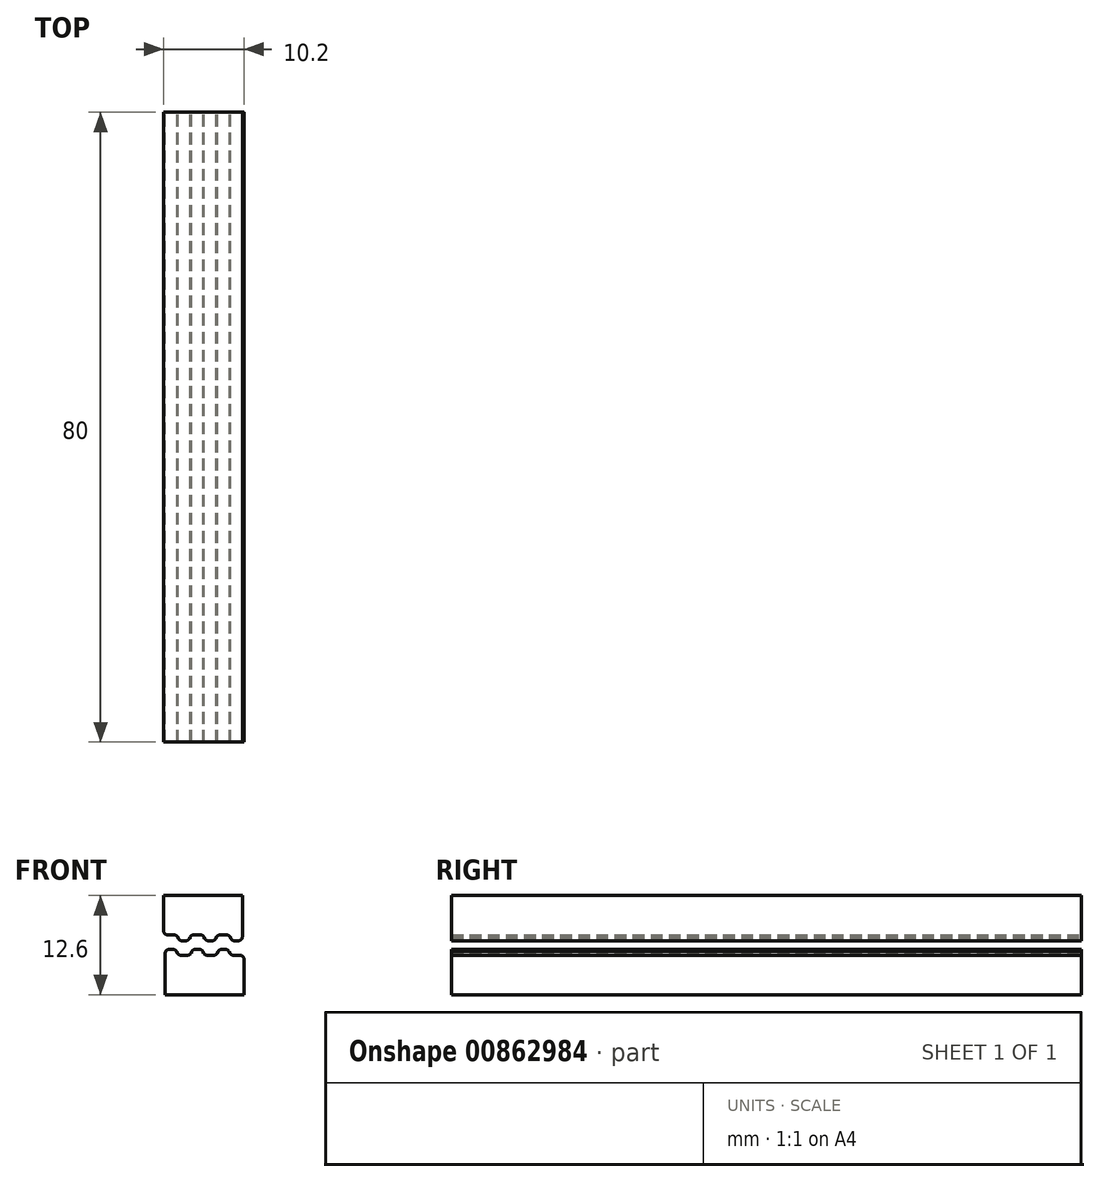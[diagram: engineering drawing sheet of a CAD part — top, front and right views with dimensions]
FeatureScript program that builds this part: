
annotation { "Feature Type Name" : "Feature", "Feature Type Description" : "" }
export const myFeature = defineFeature(function(context is Context, id is Id, definition is map)
    precondition{}
    {
        {
            var Q0;
            Q0=qCreatedBy(makeId("Front.planeOp"),FACE);
            var sketch = newSketch(context, id + "F0", { "sketchPlane" : qUnion([Q0])});
            skLineSegment(sketch, "E0", {"start": v(0, 0) * mm, "end": v(0, 5) * mm});
            skLineSegment(sketch, "E1", {"start": v(2, 5) * mm, "end": v(2.83, 5) * mm});
            skLineSegment(sketch, "E2", {"start": v(10, 4.5) * mm, "end": v(10, 0) * mm});
            skLineSegment(sketch, "E3", {"start": v(10, 0) * mm, "end": v(0, 0) * mm});
            skLineSegment(sketch, "E4.top", {"start": v(0.5, 5.75) * mm, "end": v(1, 5.75) * mm});
            skLineSegment(sketch, "E4.left", {"start": v(0, 5) * mm, "end": v(0, 5.25) * mm});
            skLineSegment(sketch, "E4.right", {"start": v(1.5, 5.25) * mm, "end": v(1.5, 5.5) * mm});
            skLineSegment(sketch, "E5.1.0.0", {"start": v(3.33, 5.25) * mm, "end": v(3.33, 5.5) * mm});
            skLineSegment(sketch, "E5.1.0.1", {"start": v(3.83, 5.75) * mm, "end": v(4.33, 5.75) * mm});
            skLineSegment(sketch, "E5.1.0.2", {"start": v(4.83, 5.25) * mm, "end": v(4.83, 5.5) * mm});
            skLineSegment(sketch, "E5.2.0.0", {"start": v(6.67, 5.25) * mm, "end": v(6.67, 5.5) * mm});
            skLineSegment(sketch, "E5.2.0.1", {"start": v(7.17, 5.75) * mm, "end": v(7.67, 5.75) * mm});
            skLineSegment(sketch, "E5.2.0.2", {"start": v(8.17, 5.25) * mm, "end": v(8.17, 5.5) * mm});
            skLineSegment(sketch, "E5.direction1", {"start": v(0, 5) * mm, "end": v(3.33, 5) * mm, "construction": true});
            skLineSegment(sketch, "E6.trimOffspring", {"start": v(5.33, 5) * mm, "end": v(6.17, 5) * mm});
            skLineSegment(sketch, "E7.trimOffspring", {"start": v(8.67, 5) * mm, "end": v(9.5, 5) * mm});
            skPoint(sketch, "E8.visualSharp", {"position": v(0, 5.75) * mm});
            skArc(sketch, "E8.filletArc", {"start": v(0.5, 5.75) * mm, "mid": v(0.15, 5.6) * mm, "end": v(0, 5.25) * mm});
            skPoint(sketch, "E9.visualSharp", {"position": v(3.33, 5.75) * mm});
            skArc(sketch, "E9.filletArc", {"start": v(3.83, 5.75) * mm, "mid": v(3.48, 5.6) * mm, "end": v(3.33, 5.25) * mm});
            skPoint(sketch, "E10.visualSharp", {"position": v(4.83, 5) * mm});
            skArc(sketch, "E10.filletArc", {"start": v(4.83, 5.5) * mm, "mid": v(4.98, 5.15) * mm, "end": v(5.33, 5) * mm});
            skPoint(sketch, "E11.visualSharp", {"position": v(4.83, 5.75) * mm});
            skArc(sketch, "E11.filletArc", {"start": v(4.83, 5.25) * mm, "mid": v(4.69, 5.6) * mm, "end": v(4.33, 5.75) * mm});
            skPoint(sketch, "E12.visualSharp", {"position": v(6.67, 5) * mm});
            skArc(sketch, "E12.filletArc", {"start": v(6.17, 5) * mm, "mid": v(6.52, 5.15) * mm, "end": v(6.67, 5.5) * mm});
            skPoint(sketch, "E13.visualSharp", {"position": v(6.67, 5.75) * mm});
            skArc(sketch, "E13.filletArc", {"start": v(7.17, 5.75) * mm, "mid": v(6.81, 5.6) * mm, "end": v(6.67, 5.25) * mm});
            skPoint(sketch, "E14.visualSharp", {"position": v(8.17, 5.75) * mm});
            skArc(sketch, "E14.filletArc", {"start": v(8.17, 5.25) * mm, "mid": v(8.02, 5.6) * mm, "end": v(7.67, 5.75) * mm});
            skPoint(sketch, "E15.visualSharp", {"position": v(8.17, 5) * mm});
            skArc(sketch, "E15.filletArc", {"start": v(8.17, 5.5) * mm, "mid": v(8.31, 5.15) * mm, "end": v(8.67, 5) * mm});
            skPoint(sketch, "E16.visualSharp", {"position": v(10, 5) * mm});
            skArc(sketch, "E16.filletArc", {"start": v(10, 4.5) * mm, "mid": v(9.85, 4.85) * mm, "end": v(9.5, 5) * mm});
            skPoint(sketch, "E17.visualSharp", {"position": v(1.5, 5.75) * mm});
            skArc(sketch, "E17.filletArc", {"start": v(1.5, 5.25) * mm, "mid": v(1.35, 5.6) * mm, "end": v(1, 5.75) * mm});
            skPoint(sketch, "E18.visualSharp", {"position": v(1.5, 5) * mm});
            skArc(sketch, "E18.filletArc", {"start": v(1.5, 5.5) * mm, "mid": v(1.65, 5.15) * mm, "end": v(2, 5) * mm});
            skPoint(sketch, "E19.visualSharp", {"position": v(3.33, 5) * mm});
            skArc(sketch, "E19.filletArc", {"start": v(2.83, 5) * mm, "mid": v(3.19, 5.15) * mm, "end": v(3.33, 5.5) * mm});
            skSolve(sketch);
        }
        {
            var Q0;
            Q0=makeQuery(id+"F0.imprint","IMPRINT",FACE,{"disambiguationData":[TD([[makeQuery(id+"F0.imprint","IMPRINT",EDGE,{"derivedFrom":sQuery(id+"F0.wireOp",EDGE,"E0")}),-1.0]])]});
            extrude(context, id + "F1", {"entities" : qUnion([Q0]), "depth" : 80 * mm, "offsetDistance" : 25 * mm});
        }
        {
            var Q0;
            Q0=makeQuery(id+"F1.opExtrude","SWEPT_BODY",BODY,{"disambiguationData":[OSD([sQuery(id+"F0.wireOp",EDGE,"E0"),sQuery(id+"F0.wireOp",EDGE,"E1"),sQuery(id+"F0.wireOp",EDGE,"E2"),sQuery(id+"F0.wireOp",EDGE,"E3"),sQuery(id+"F0.wireOp",EDGE,"E4.top"),sQuery(id+"F0.wireOp",EDGE,"E4.left"),sQuery(id+"F0.wireOp",EDGE,"E5.1.0.1"),sQuery(id+"F0.wireOp",EDGE,"E5.2.0.1"),sQuery(id+"F0.wireOp",EDGE,"E6.trimOffspring"),sQuery(id+"F0.wireOp",EDGE,"E7.trimOffspring"),sQuery(id+"F0.wireOp",EDGE,"E8.filletArc"),sQuery(id+"F0.wireOp",EDGE,"E9.filletArc"),sQuery(id+"F0.wireOp",EDGE,"E10.filletArc"),sQuery(id+"F0.wireOp",EDGE,"E11.filletArc"),sQuery(id+"F0.wireOp",EDGE,"E12.filletArc"),sQuery(id+"F0.wireOp",EDGE,"E13.filletArc"),sQuery(id+"F0.wireOp",EDGE,"E14.filletArc"),sQuery(id+"F0.wireOp",EDGE,"E15.filletArc"),sQuery(id+"F0.wireOp",EDGE,"E16.filletArc"),sQuery(id+"F0.wireOp",EDGE,"E17.filletArc"),sQuery(id+"F0.wireOp",EDGE,"E18.filletArc"),sQuery(id+"F0.wireOp",EDGE,"E19.filletArc")])]});
            transform(context, id + "F2", {"entities" : qUnion([Q0]), "transformType" : TransformType.TRANSLATION_3D, "dx" : 0 * mm, "dy" : 0 * mm, "dz" : 17.5 * mm, "makeCopy" : true});
        }
        {
            var Q0;
            Q0=makeQuery(id+"F2.opPattern","COPY",BODY,{"derivedFrom":makeQuery(id+"F1.opExtrude","SWEPT_BODY",BODY,{"disambiguationData":[OSD([sQuery(id+"F0.wireOp",EDGE,"E0"),sQuery(id+"F0.wireOp",EDGE,"E1"),sQuery(id+"F0.wireOp",EDGE,"E2"),sQuery(id+"F0.wireOp",EDGE,"E3"),sQuery(id+"F0.wireOp",EDGE,"E4.top"),sQuery(id+"F0.wireOp",EDGE,"E4.left"),sQuery(id+"F0.wireOp",EDGE,"E5.1.0.1"),sQuery(id+"F0.wireOp",EDGE,"E5.2.0.1"),sQuery(id+"F0.wireOp",EDGE,"E6.trimOffspring"),sQuery(id+"F0.wireOp",EDGE,"E7.trimOffspring"),sQuery(id+"F0.wireOp",EDGE,"E8.filletArc"),sQuery(id+"F0.wireOp",EDGE,"E9.filletArc"),sQuery(id+"F0.wireOp",EDGE,"E10.filletArc"),sQuery(id+"F0.wireOp",EDGE,"E11.filletArc"),sQuery(id+"F0.wireOp",EDGE,"E12.filletArc"),sQuery(id+"F0.wireOp",EDGE,"E13.filletArc"),sQuery(id+"F0.wireOp",EDGE,"E14.filletArc"),sQuery(id+"F0.wireOp",EDGE,"E15.filletArc"),sQuery(id+"F0.wireOp",EDGE,"E16.filletArc"),sQuery(id+"F0.wireOp",EDGE,"E17.filletArc"),sQuery(id+"F0.wireOp",EDGE,"E18.filletArc"),sQuery(id+"F0.wireOp",EDGE,"E19.filletArc")])]}),"instanceName":"1"});
            var Q1;
            Q1=makeQuery(id+"F1.opExtrude","SWEPT_EDGE",EDGE,{"disambiguationData":[OSD([sQuery(id+"F0.wireOp",EDGE,"E2"),sQuery(id+"F0.wireOp",EDGE,"E3")])]});
            transform(context, id + "F3", {"entities" : qUnion([Q0]), "transformType" : TransformType.ROTATION, "transformAxis" : qUnion([Q1]), "angle" : 180 * degree, "makeCopy" : false});
        }
        {
            var Q0;
            Q0=makeQuery(id+"F2.opPattern","COPY",BODY,{"derivedFrom":makeQuery(id+"F1.opExtrude","SWEPT_BODY",BODY,{"disambiguationData":[OSD([sQuery(id+"F0.wireOp",EDGE,"E0"),sQuery(id+"F0.wireOp",EDGE,"E1"),sQuery(id+"F0.wireOp",EDGE,"E2"),sQuery(id+"F0.wireOp",EDGE,"E3"),sQuery(id+"F0.wireOp",EDGE,"E4.top"),sQuery(id+"F0.wireOp",EDGE,"E4.left"),sQuery(id+"F0.wireOp",EDGE,"E5.1.0.1"),sQuery(id+"F0.wireOp",EDGE,"E5.2.0.1"),sQuery(id+"F0.wireOp",EDGE,"E6.trimOffspring"),sQuery(id+"F0.wireOp",EDGE,"E7.trimOffspring"),sQuery(id+"F0.wireOp",EDGE,"E8.filletArc"),sQuery(id+"F0.wireOp",EDGE,"E9.filletArc"),sQuery(id+"F0.wireOp",EDGE,"E10.filletArc"),sQuery(id+"F0.wireOp",EDGE,"E11.filletArc"),sQuery(id+"F0.wireOp",EDGE,"E12.filletArc"),sQuery(id+"F0.wireOp",EDGE,"E13.filletArc"),sQuery(id+"F0.wireOp",EDGE,"E14.filletArc"),sQuery(id+"F0.wireOp",EDGE,"E15.filletArc"),sQuery(id+"F0.wireOp",EDGE,"E16.filletArc"),sQuery(id+"F0.wireOp",EDGE,"E17.filletArc"),sQuery(id+"F0.wireOp",EDGE,"E18.filletArc"),sQuery(id+"F0.wireOp",EDGE,"E19.filletArc")])]}),"instanceName":"1"});
            transform(context, id + "F4", {"entities" : qUnion([Q0]), "transformType" : TransformType.TRANSLATION_3D, "dx" : -10.2 * mm, "dy" : 0 * mm, "dz" : 30.1 * mm, "makeCopy" : false});
        }
    });
